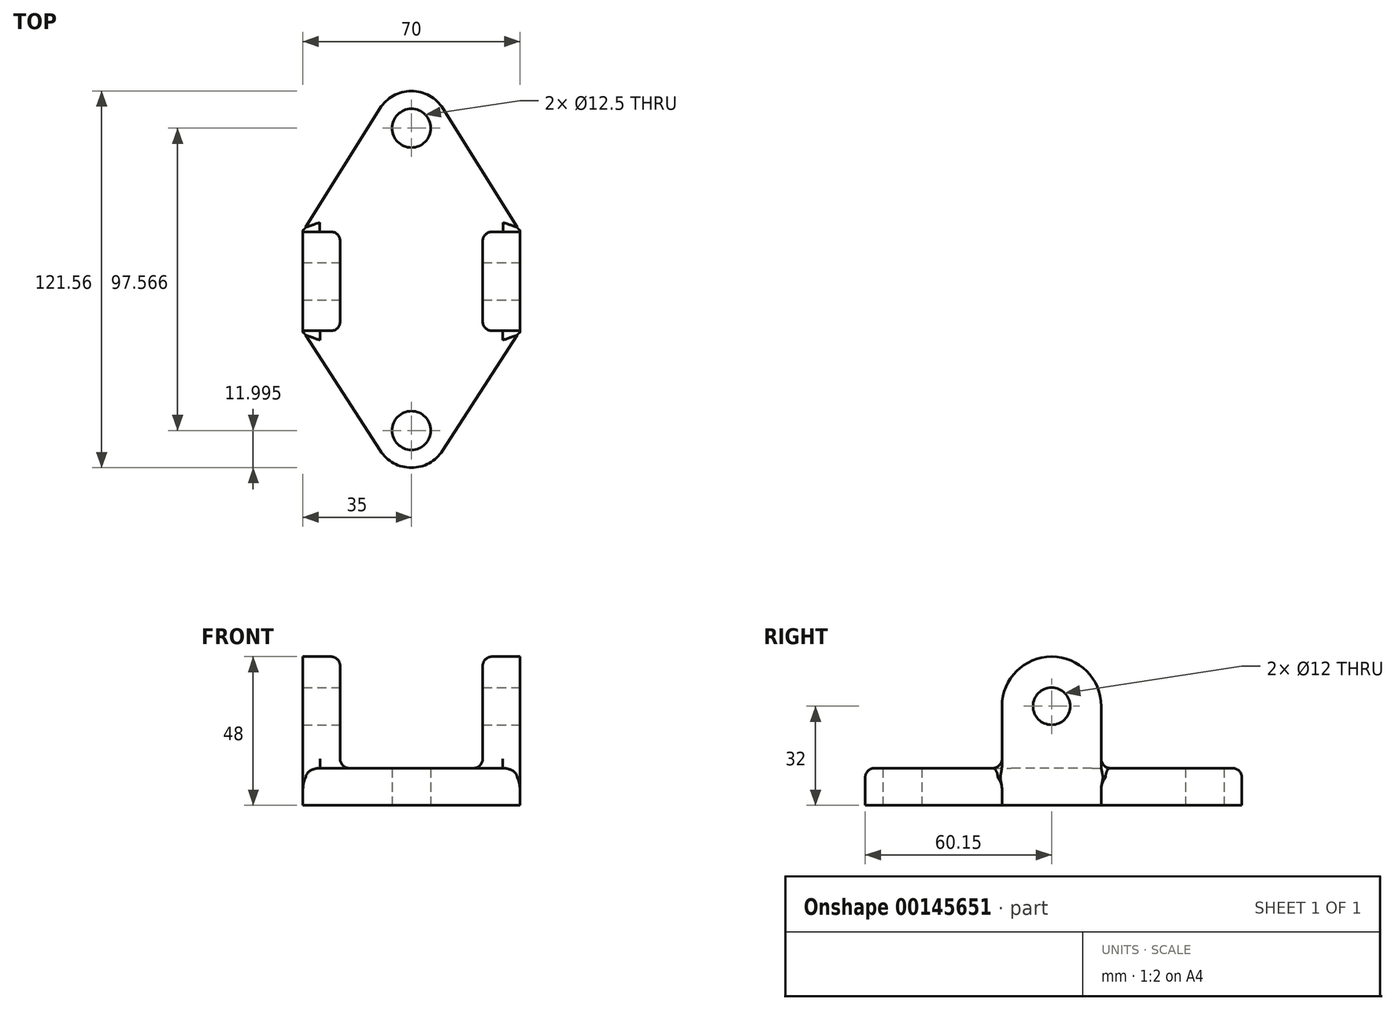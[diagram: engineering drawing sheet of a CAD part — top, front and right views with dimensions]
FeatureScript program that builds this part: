
annotation { "Feature Type Name" : "Feature", "Feature Type Description" : "" }
export const myFeature = defineFeature(function(context is Context, id is Id, definition is map)
    precondition{}
    {
        {
            var Q0;
            Q0=qCreatedBy(makeId("Right.planeOp"),FACE);
            var sketch = newSketch(context, id + "F0", { "sketchPlane" : qUnion([Q0])});
            skLineSegment(sketch, "E0", {"start": v(-16, 0) * mm, "end": v(-16, 32) * mm});
            skLineSegment(sketch, "E1", {"start": v(-16, 0) * mm, "end": v(16, 0) * mm});
            skLineSegment(sketch, "E2", {"start": v(16, 0) * mm, "end": v(16, 32) * mm});
            skCircle(sketch, "E3", {"center": v(0, 32) * mm, "radius": 6 * mm});
            skArc(sketch, "E4", {"start": v(16, 32) * mm, "mid": v(0, 48) * mm, "end": v(-16, 32) * mm});
            skSolve(sketch);
        }
        {
            var Q0;
            Q0=qSketchRegion(id+"F0",true);
            extrude(context, id + "F1", {"entities" : qUnion([Q0]), "oppositeDirection" : true, "depth" : 12 * mm});
        }
        {
            var Q0;
            Q0=qCreatedBy(makeId("Top.planeOp"),FACE);
            var sketch = newSketch(context, id + "F2", { "sketchPlane" : qUnion([Q0])});
            skPoint(sketch, "E5.0", {"position": v(-12, 16) * mm});
            skPoint(sketch, "E6.0", {"position": v(-12, -16) * mm});
            skCircle(sketch, "E7", {"center": v(23, 49.41) * mm, "radius": 6.25 * mm});
            skArc(sketch, "E8", {"start": v(33.18, 55.77) * mm, "mid": v(23, 61.41) * mm, "end": v(12.82, 55.77) * mm});
            skLineSegment(sketch, "E9", {"start": v(33.18, 55.77) * mm, "end": v(58, 16) * mm});
            skPoint(sketch, "E10", {"position": v(-12, 0) * mm});
            skPoint(sketch, "E11", {"position": v(58, 0) * mm});
            skLineSegment(sketch, "E12", {"start": v(58, 0) * mm, "end": v(58, -16) * mm});
            skLineSegment(sketch, "E13", {"start": v(58, -16) * mm, "end": v(58, 16) * mm});
            skPoint(sketch, "E14", {"position": v(23, 0) * mm});
            skLineSegment(sketch, "E15", {"start": v(23, 74.76) * mm, "end": v(23, -48.15) * mm, "construction": true});
            skLineSegment(sketch, "E16", {"start": v(-12, 16) * mm, "end": v(12.82, 55.77) * mm});
            skCircle(sketch, "E17", {"center": v(23, -48.15) * mm, "radius": 6.25 * mm});
            skArc(sketch, "E18", {"start": v(12.91, -54.66) * mm, "mid": v(23, -60.15) * mm, "end": v(33.09, -54.66) * mm});
            skLineSegment(sketch, "E19", {"start": v(58, -16) * mm, "end": v(33.09, -54.66) * mm});
            skLineSegment(sketch, "E20", {"start": v(12.91, -54.66) * mm, "end": v(-12, -16) * mm});
            skLineSegment(sketch, "E21", {"start": v(-12, -16) * mm, "end": v(-12, 16) * mm});
            skSolve(sketch);
        }
        {
            var Q0;
            Q0=qSketchRegion(id+"F2",true);
            extrude(context, id + "F3", {"entities" : qUnion([Q0]), "operationType" : NewBodyOperationType.ADD, "depth" : 12 * mm});
        }
        {
            var Q0;
            Q0=makeQuery(id+"F3.opExtrude","SWEPT_FACE",FACE,{"disambiguationData":[OSD([sQuery(id+"F2.wireOp",EDGE,"E13")])]});
            var sketch = newSketch(context, id + "F4", { "sketchPlane" : qUnion([Q0])});
            skLineSegment(sketch, "E22.0.0", {"start": v(-16, 0) * mm, "end": v(-16, 12) * mm});
            skLineSegment(sketch, "E22.0.1", {"start": v(-16, 12) * mm, "end": v(-16, 32) * mm});
            skArc(sketch, "E22.0.2", {"start": v(-16, 32) * mm, "mid": v(0, 48) * mm, "end": v(16, 32) * mm});
            skLineSegment(sketch, "E22.0.3", {"start": v(16, 32) * mm, "end": v(16, 12) * mm});
            skLineSegment(sketch, "E22.0.4", {"start": v(16, 12) * mm, "end": v(16, 0) * mm});
            skLineSegment(sketch, "E22.0.5", {"start": v(16, 0) * mm, "end": v(-16, 0) * mm});
            skCircle(sketch, "E23.0", {"center": v(0, 32) * mm, "radius": 6 * mm});
            skSolve(sketch);
        }
        {
            var Q0;
            Q0=qSketchRegion(id+"F4",true);
            extrude(context, id + "F5", {"entities" : qUnion([Q0]), "operationType" : NewBodyOperationType.ADD, "oppositeDirection" : true, "depth" : 12 * mm});
        }
        {
            var Q0;
            Q0=makeQuery(id+"F3.opExtrude","CAP_EDGE",EDGE,{"disambiguationData":[OSD([sQuery(id+"F2.wireOp",EDGE,"E19")])],"isStart":false});
            var Q1;
            Q1=makeQuery(id+"F3.opExtrude","CAP_EDGE",EDGE,{"disambiguationData":[OSD([sQuery(id+"F2.wireOp",EDGE,"E9")])],"isStart":false});
            var Q2;
            Q2=makeQuery(id+"F5.opExtrude","CAP_EDGE",EDGE,{"disambiguationData":[OSD([sQuery(id+"F4.wireOp",EDGE,"E22.0.2")])],"isStart":false});
            var Q3;
            Q3=makeQuery(id+"F1.opExtrude","CAP_EDGE",EDGE,{"disambiguationData":[OSD([sQuery(id+"F0.wireOp",EDGE,"E4")])],"isStart":true});
            fillet(context, id + "F6", {"entities" : qUnion([Q0, Q1, Q2, Q3]), "radius" : 3 * mm, "tangentPropagation" : true, "allowEdgeOverflow" : false});
        }
        {
            var Q0;
            Q0=makeQuery(id+"F5.boolean.opBoolean","INTERSECT",EDGE,{"derivedFrom":[makeQuery(id+"F3.opExtrude","CAP_FACE",FACE,{"disambiguationData":[OSD([sQuery(id+"F2.wireOp",EDGE,"E7"),sQuery(id+"F2.wireOp",EDGE,"E8"),sQuery(id+"F2.wireOp",EDGE,"E9"),sQuery(id+"F2.wireOp",EDGE,"E13"),sQuery(id+"F2.wireOp",EDGE,"E16"),sQuery(id+"F2.wireOp",EDGE,"E17"),sQuery(id+"F2.wireOp",EDGE,"E18"),sQuery(id+"F2.wireOp",EDGE,"E19"),sQuery(id+"F2.wireOp",EDGE,"E20"),sQuery(id+"F2.wireOp",EDGE,"E21")])],"isStart":false}),makeQuery(id+"F5.opExtrude","SWEPT_FACE",FACE,{"disambiguationData":[OSD([sQuery(id+"F4.wireOp",EDGE,"E22.0.0"),sQuery(id+"F4.wireOp",EDGE,"E22.0.1")])]})]});
            var Q1;
            Q1=makeQuery(id+"F3.boolean.opBoolean","INTERSECT",EDGE,{"derivedFrom":[makeQuery(id+"F1.opExtrude","SWEPT_FACE",FACE,{"disambiguationData":[OSD([sQuery(id+"F0.wireOp",EDGE,"E0")])]}),makeQuery(id+"F3.opExtrude","CAP_FACE",FACE,{"disambiguationData":[OSD([sQuery(id+"F2.wireOp",EDGE,"E7"),sQuery(id+"F2.wireOp",EDGE,"E8"),sQuery(id+"F2.wireOp",EDGE,"E9"),sQuery(id+"F2.wireOp",EDGE,"E13"),sQuery(id+"F2.wireOp",EDGE,"E16"),sQuery(id+"F2.wireOp",EDGE,"E17"),sQuery(id+"F2.wireOp",EDGE,"E18"),sQuery(id+"F2.wireOp",EDGE,"E19"),sQuery(id+"F2.wireOp",EDGE,"E20"),sQuery(id+"F2.wireOp",EDGE,"E21")])],"isStart":false})]});
            fillet(context, id + "F7", {"entities" : qUnion([Q0, Q1]), "radius" : 3 * mm, "tangentPropagation" : true, "allowEdgeOverflow" : false});
        }
    });
